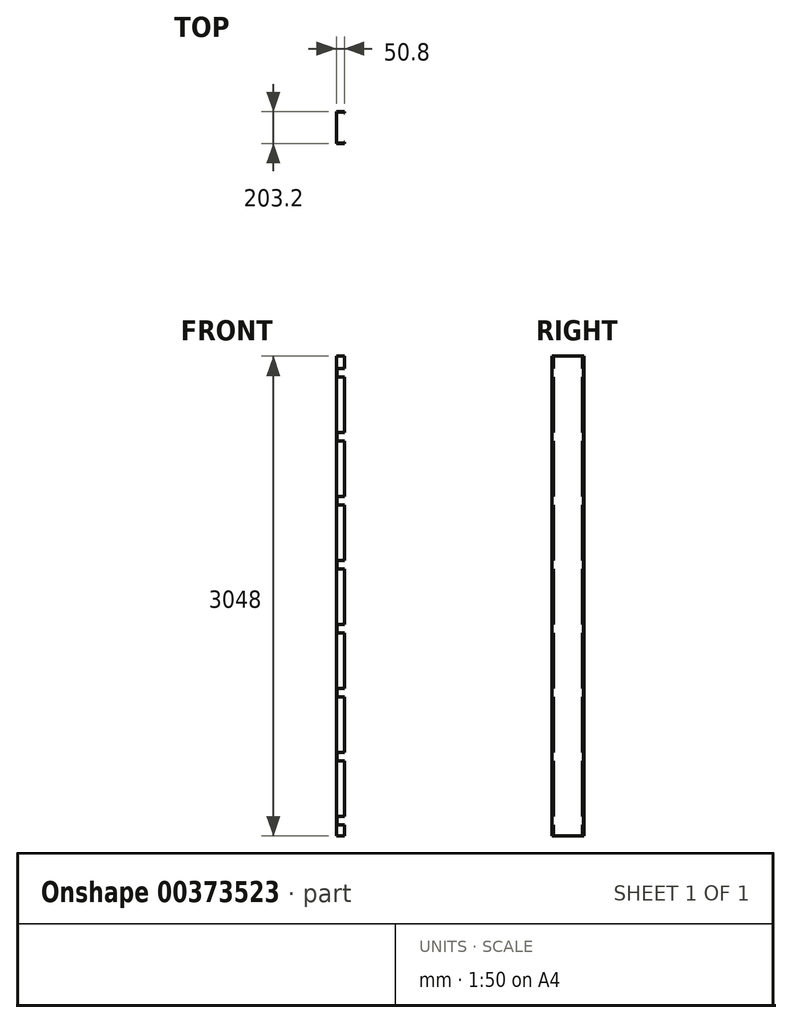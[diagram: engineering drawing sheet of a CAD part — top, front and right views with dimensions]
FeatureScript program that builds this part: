
annotation { "Feature Type Name" : "Feature", "Feature Type Description" : "" }
export const myFeature = defineFeature(function(context is Context, id is Id, definition is map)
    precondition{}
    {
        {
            var Q0;
            Q0=qCreatedBy(makeId("Top.planeOp"),FACE);
            var sketch = newSketch(context, id + "F0", { "sketchPlane" : qUnion([Q0])});
            skLineSegment(sketch, "E0", {"start": v(25.4, 92.08) * mm, "end": v(25.4, 101.6) * mm});
            skLineSegment(sketch, "E1", {"start": v(25.4, 101.6) * mm, "end": v(-25.4, 101.6) * mm});
            skLineSegment(sketch, "E2", {"start": v(-25.4, 101.6) * mm, "end": v(-25.4, -101.6) * mm});
            skLineSegment(sketch, "E3", {"start": v(-25.4, -101.6) * mm, "end": v(25.4, -101.6) * mm});
            skLineSegment(sketch, "E4", {"start": v(25.4, -101.6) * mm, "end": v(25.4, -92.08) * mm});
            skLineSegment(sketch, "E5.0", {"start": v(25.4, 99.99) * mm, "end": v(-25.4, 99.99) * mm});
            skLineSegment(sketch, "E6.0", {"start": v(-23.79, 101.6) * mm, "end": v(-23.79, -101.6) * mm});
            skLineSegment(sketch, "E7.0", {"start": v(-25.4, -99.99) * mm, "end": v(25.4, -99.99) * mm});
            skLineSegment(sketch, "E8.0", {"start": v(23.79, -101.6) * mm, "end": v(23.79, -92.08) * mm});
            skLineSegment(sketch, "E9", {"start": v(23.79, -92.08) * mm, "end": v(25.4, -92.08) * mm});
            skLineSegment(sketch, "E10.0", {"start": v(23.79, 92.08) * mm, "end": v(23.79, 101.6) * mm});
            skLineSegment(sketch, "E11", {"start": v(23.79, 92.08) * mm, "end": v(25.4, 92.08) * mm});
            skSolve(sketch);
        }
        {
            var Q0;
            Q0=qSketchRegion(id+"F0",true);
            extrude(context, id + "F1", {"entities" : qUnion([Q0]), "depth" : 3048 * mm});
        }
        {
            var Q0;
            Q0=makeQuery(id+"F1.opExtrude","SWEPT_FACE",FACE,{"disambiguationData":[OSD([sQuery(id+"F0.wireOp",EDGE,"E3")])]});
            var sketch = newSketch(context, id + "F2", { "sketchPlane" : qUnion([Q0])});
            skLineSegment(sketch, "E12.bottom", {"start": v(25.4, 2968.01) * mm, "end": v(-22.23, 2968.01) * mm});
            skLineSegment(sketch, "E12.top", {"start": v(25.4, 2914.04) * mm, "end": v(-22.22, 2914.04) * mm});
            skLineSegment(sketch, "E12.left", {"start": v(25.4, 2968.01) * mm, "end": v(25.4, 2914.04) * mm});
            skLineSegment(sketch, "E12.right", {"start": v(-22.23, 2968.01) * mm, "end": v(-22.22, 2914.04) * mm});
            skLineSegment(sketch, "E13.0.1.0", {"start": v(25.4, 2507.64) * mm, "end": v(-22.22, 2507.64) * mm});
            skLineSegment(sketch, "E13.0.1.1", {"start": v(25.4, 2561.61) * mm, "end": v(-22.23, 2561.61) * mm});
            skLineSegment(sketch, "E13.0.1.2", {"start": v(25.4, 2561.61) * mm, "end": v(25.4, 2507.64) * mm});
            skLineSegment(sketch, "E13.0.1.3", {"start": v(-22.23, 2561.61) * mm, "end": v(-22.22, 2507.64) * mm});
            skLineSegment(sketch, "E13.0.2.0", {"start": v(25.4, 2101.24) * mm, "end": v(-22.22, 2101.24) * mm});
            skLineSegment(sketch, "E13.0.2.1", {"start": v(25.4, 2155.21) * mm, "end": v(-22.23, 2155.21) * mm});
            skLineSegment(sketch, "E13.0.2.2", {"start": v(25.4, 2155.21) * mm, "end": v(25.4, 2101.24) * mm});
            skLineSegment(sketch, "E13.0.2.3", {"start": v(-22.23, 2155.21) * mm, "end": v(-22.22, 2101.24) * mm});
            skLineSegment(sketch, "E13.0.3.0", {"start": v(25.4, 1694.84) * mm, "end": v(-22.22, 1694.84) * mm});
            skLineSegment(sketch, "E13.0.3.1", {"start": v(25.4, 1748.81) * mm, "end": v(-22.23, 1748.81) * mm});
            skLineSegment(sketch, "E13.0.3.2", {"start": v(25.4, 1748.81) * mm, "end": v(25.4, 1694.84) * mm});
            skLineSegment(sketch, "E13.0.3.3", {"start": v(-22.23, 1748.81) * mm, "end": v(-22.22, 1694.84) * mm});
            skLineSegment(sketch, "E13.0.4.0", {"start": v(25.4, 1288.44) * mm, "end": v(-22.22, 1288.44) * mm});
            skLineSegment(sketch, "E13.0.4.1", {"start": v(25.4, 1342.41) * mm, "end": v(-22.23, 1342.41) * mm});
            skLineSegment(sketch, "E13.0.4.2", {"start": v(25.4, 1342.41) * mm, "end": v(25.4, 1288.44) * mm});
            skLineSegment(sketch, "E13.0.4.3", {"start": v(-22.23, 1342.41) * mm, "end": v(-22.22, 1288.44) * mm});
            skLineSegment(sketch, "E13.0.5.0", {"start": v(25.4, 882.04) * mm, "end": v(-22.22, 882.04) * mm});
            skLineSegment(sketch, "E13.0.5.1", {"start": v(25.4, 936.01) * mm, "end": v(-22.23, 936.01) * mm});
            skLineSegment(sketch, "E13.0.5.2", {"start": v(25.4, 936.01) * mm, "end": v(25.4, 882.04) * mm});
            skLineSegment(sketch, "E13.0.5.3", {"start": v(-22.23, 936.01) * mm, "end": v(-22.22, 882.04) * mm});
            skLineSegment(sketch, "E13.0.6.0", {"start": v(25.4, 475.64) * mm, "end": v(-22.22, 475.64) * mm});
            skLineSegment(sketch, "E13.0.6.1", {"start": v(25.4, 529.61) * mm, "end": v(-22.23, 529.61) * mm});
            skLineSegment(sketch, "E13.0.6.2", {"start": v(25.4, 529.61) * mm, "end": v(25.4, 475.64) * mm});
            skLineSegment(sketch, "E13.0.6.3", {"start": v(-22.23, 529.61) * mm, "end": v(-22.22, 475.64) * mm});
            skLineSegment(sketch, "E13.0.7.0", {"start": v(25.4, 69.24) * mm, "end": v(-22.22, 69.24) * mm});
            skLineSegment(sketch, "E13.0.7.1", {"start": v(25.4, 123.21) * mm, "end": v(-22.23, 123.21) * mm});
            skLineSegment(sketch, "E13.0.7.2", {"start": v(25.4, 123.21) * mm, "end": v(25.4, 69.24) * mm});
            skLineSegment(sketch, "E13.0.7.3", {"start": v(-22.23, 123.21) * mm, "end": v(-22.22, 69.24) * mm});
            skLineSegment(sketch, "E13.direction1", {"start": v(-22.22, 2914.04) * mm, "end": v(3.18, 2914.04) * mm, "construction": true});
            skLineSegment(sketch, "E13.direction2", {"start": v(-22.22, 2914.04) * mm, "end": v(-22.22, 2507.64) * mm, "construction": true});
            skSolve(sketch);
        }
        {
            var Q0;
            Q0 = qSketchRegion(id + "F2", true);
            extrude(context, id + "F3", {"entities" : qUnion([Q0]), "operationType" : NewBodyOperationType.REMOVE, "endBound" : BoundingType.THROUGH_ALL, "oppositeDirection" : true, "depth" : 25.4 * mm});
        }
    });
